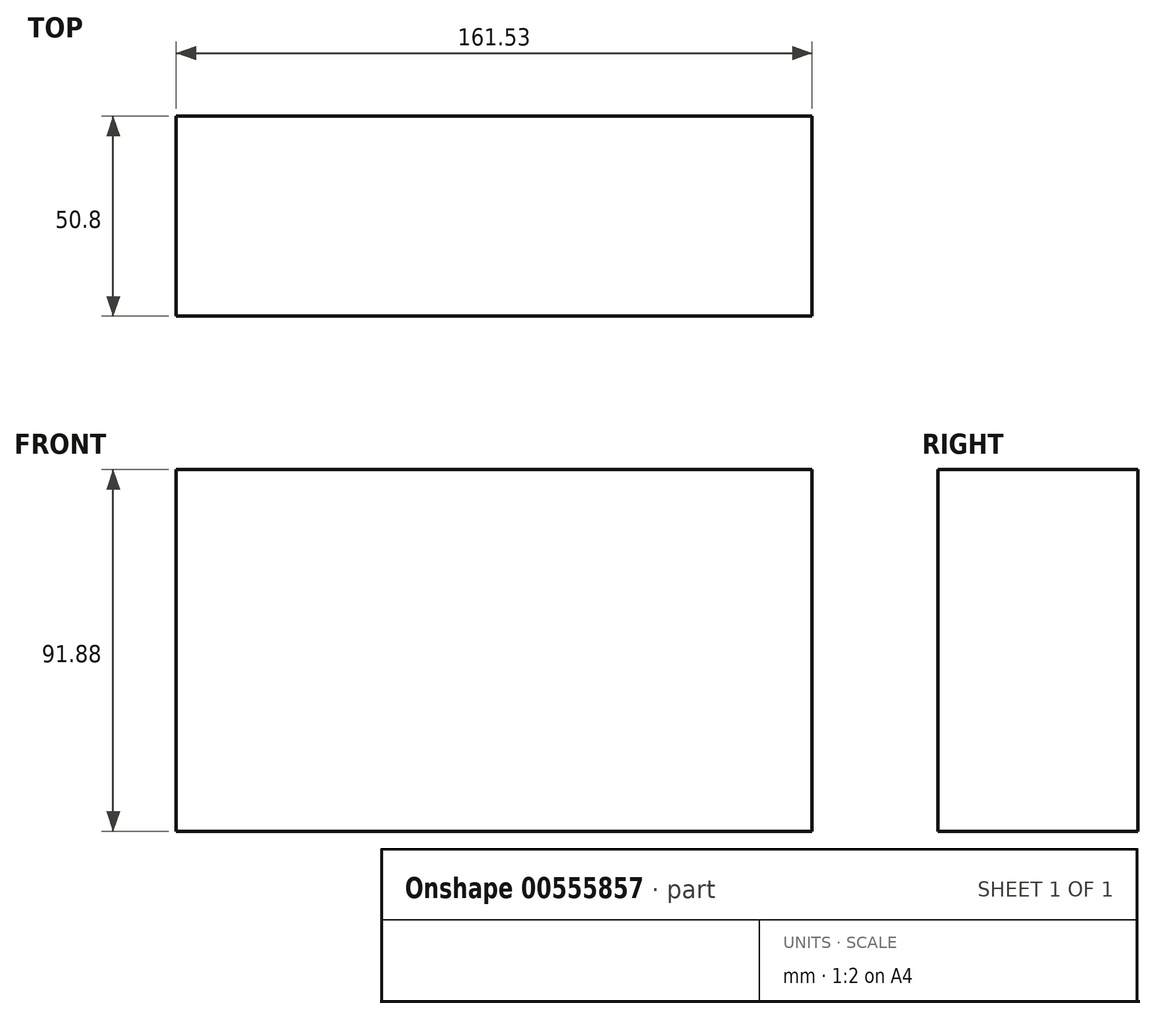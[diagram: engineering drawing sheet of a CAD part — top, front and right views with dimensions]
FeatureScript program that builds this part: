
annotation { "Feature Type Name" : "Feature", "Feature Type Description" : "" }
export const myFeature = defineFeature(function(context is Context, id is Id, definition is map)
    precondition{}
    {
        {
            var Q0;
            Q0=qCreatedBy(makeId("Front.planeOp"),FACE);
            var sketch = newSketch(context, id + "F0", { "sketchPlane" : qUnion([Q0])});
            skLineSegment(sketch, "E0.bottom", {"start": v(-69.83, 60.8) * mm, "end": v(91.7, 60.8) * mm});
            skLineSegment(sketch, "E0.top", {"start": v(-69.83, -31.08) * mm, "end": v(91.7, -31.08) * mm});
            skLineSegment(sketch, "E0.left", {"start": v(-69.83, 60.8) * mm, "end": v(-69.83, -31.08) * mm});
            skLineSegment(sketch, "E0.right", {"start": v(91.7, 60.8) * mm, "end": v(91.7, -31.08) * mm});
            skSolve(sketch);
        }
        {
            var Q0;
            Q0=makeQuery(id+"F0.imprint","IMPRINT",FACE,{"disambiguationData":[TD([[makeQuery(id+"F0.imprint","IMPRINT",EDGE,{"derivedFrom":sQuery(id+"F0.wireOp",EDGE,"E0.bottom")}),-1.0]])]});
            extrude(context, id + "F1", {"entities" : qUnion([Q0]), "depth" : 50.8 * mm, "offsetDistance" : 25.4 * mm});
        }
    });
